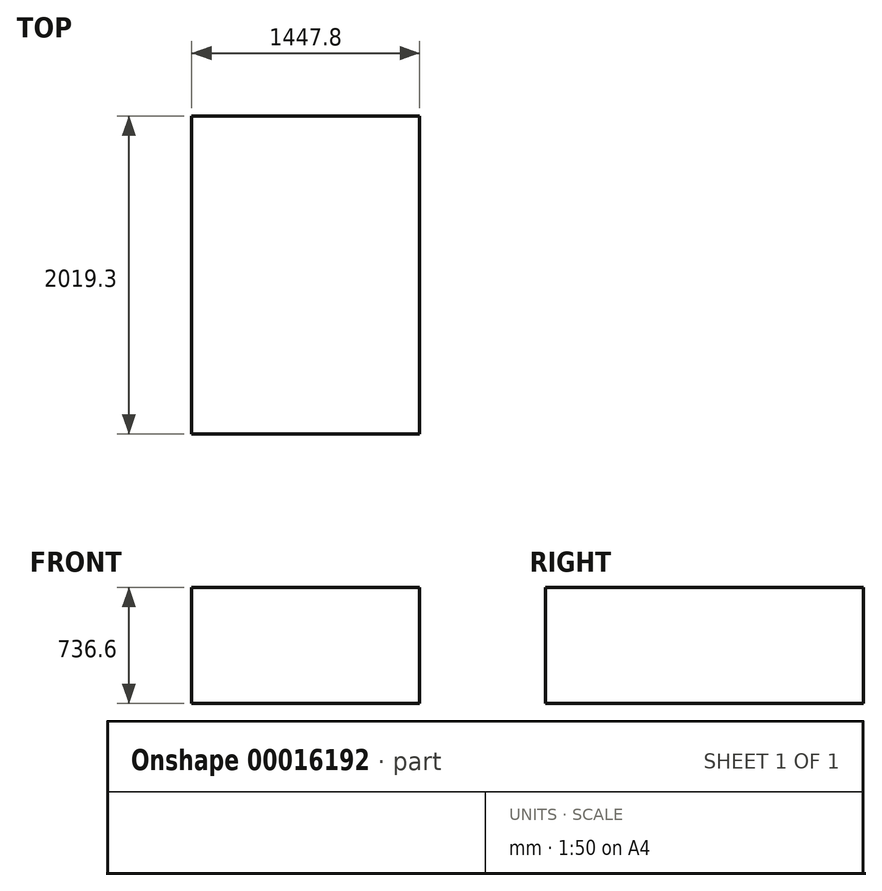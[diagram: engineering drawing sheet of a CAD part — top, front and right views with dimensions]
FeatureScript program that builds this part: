
annotation { "Feature Type Name" : "Feature", "Feature Type Description" : "" }
export const myFeature = defineFeature(function(context is Context, id is Id, definition is map)
    precondition{}
    {
        {
            var Q0;
            Q0=qCreatedBy(makeId("Top.planeOp"),FACE);
            var sketch = newSketch(context, id + "F0", { "sketchPlane" : qUnion([Q0])});
            skLineSegment(sketch, "E0.rect.bottom", {"start": v(723.9, 1009.65) * mm, "end": v(-723.9, 1009.65) * mm});
            skLineSegment(sketch, "E0.rect.top", {"start": v(723.9, -1009.65) * mm, "end": v(-723.9, -1009.65) * mm});
            skLineSegment(sketch, "E0.rect.left", {"start": v(723.9, 1009.65) * mm, "end": v(723.9, -1009.65) * mm});
            skLineSegment(sketch, "E0.rect.right", {"start": v(-723.9, 1009.65) * mm, "end": v(-723.9, -1009.65) * mm});
            skPoint(sketch, "E0.rect.middle", {"position": v(0, 0) * mm});
            skSolve(sketch);
        }
        {
            var Q0;
            Q0 = qSketchRegion(id + "F0", true);
            extrude(context, id + "F1", {"entities" : qUnion([Q0]), "depth" : 736.6 * mm});
        }
    });
